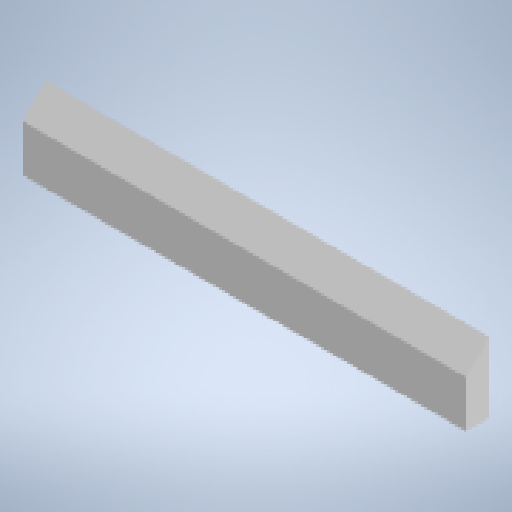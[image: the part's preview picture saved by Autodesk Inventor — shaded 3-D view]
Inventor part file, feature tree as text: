
AUTODESK INVENTOR PART (.ipt)
format: ipt  version: 2023 (Build 270158000, 158)  size: 125,440 bytes
history: native  units: in
note: dims shown in document units (in); Inventor stores cm internally (conversion verified against a paired STEP export)
features: extrude x1, sketch x1
ambient origin geometry x8: Origin, YZ Plane, XZ Plane, XY Plane, X Axis, Y Axis, Z Axis, Center Point
bodies: Solid1 (feature_tree)
feature tree (2):
  extrude  "Extrusion1"  Depth=0.1969in
  sketch  "Sketch1"  dims[d0=0.5906in d1=0.1969in d2=0.1969in d3=3.5433in d4=0.1969in d5=0.0in d6=0.0in]
